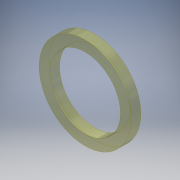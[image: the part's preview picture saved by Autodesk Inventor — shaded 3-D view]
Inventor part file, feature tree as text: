
AUTODESK INVENTOR PART (.ipt)
format: ipt  version: 2019.4 (Build 234330000, 330)  size: 103,936 bytes
history: native  units: mm
features: extrude x1, sketch x1
ambient origin geometry x8: Origin, YZ Plane, XZ Plane, XY Plane, X Axis, Y Axis, Z Axis, Center Point
bodies: Solid1 (feature_tree)
feature tree (2):
  extrude  "Extrusion1"  Depth=7.0mm
  sketch  "Sketch1"  dims[d0=65.0mm d1=50.0mm d2=7.0mm d3=0.0mm]
